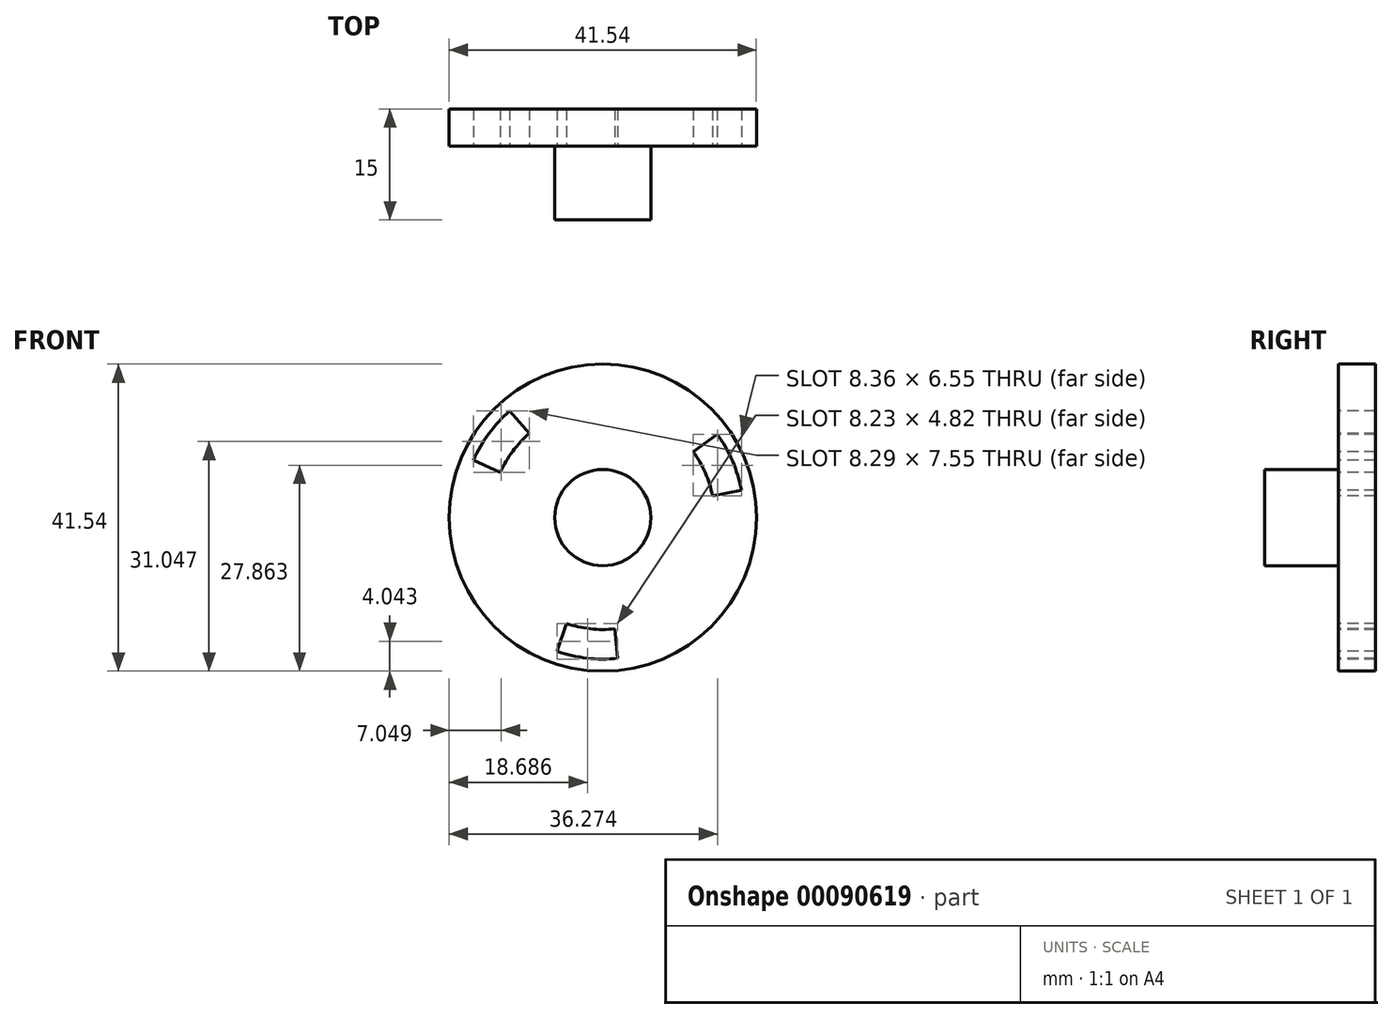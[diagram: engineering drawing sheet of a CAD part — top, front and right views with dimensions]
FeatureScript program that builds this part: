
annotation { "Feature Type Name" : "Feature", "Feature Type Description" : "" }
export const myFeature = defineFeature(function(context is Context, id is Id, definition is map)
    precondition{}
    {
        {
            var Q0;
            Q0=qCreatedBy(makeId("Front.planeOp"),FACE);
            var sketch = newSketch(context, id + "F0", { "sketchPlane" : qUnion([Q0])});
            skCircle(sketch, "E0", {"center": v(0, 0) * mm, "radius": 6.5 * mm});
            skSolve(sketch);
        }
        {
            var Q0;
            Q0 = qSketchRegion(id + "F0", true);
            extrude(context, id + "F1", {"entities" : qUnion([Q0]), "depth" : 10 * mm});
        }
        {
            var Q0;
            Q0=qCreatedBy(makeId("Front.planeOp"),FACE);
            var sketch = newSketch(context, id + "F2", { "sketchPlane" : qUnion([Q0])});
            skCircle(sketch, "E1", {"center": v(0, 0) * mm, "radius": 20.77 * mm});
            skSolve(sketch);
        }
        {
            var Q0;
            Q0=makeQuery(id+"F2.imprint","IMPRINT",FACE,{"disambiguationData":[TD([[makeQuery(id+"F2.imprint","IMPRINT",EDGE,{"derivedFrom":sQuery(id+"F2.wireOp",EDGE,"E1")}),1.0]])]});
            extrude(context, id + "F3", {"entities" : qUnion([Q0]), "operationType" : NewBodyOperationType.ADD, "oppositeDirection" : true, "depth" : 5 * mm});
        }
        {
            var Q0;
            Q0=makeQuery(id+"F3.opExtrude","CAP_FACE",FACE,{"disambiguationData":[OSD([sQuery(id+"F2.wireOp",EDGE,"E1")])],"isStart":true});
            var sketch = newSketch(context, id + "F4", { "sketchPlane" : qUnion([Q0])});
            skCircle(sketch, "E2", {"center": v(0, 0) * mm, "radius": 19.14 * mm});
            skCircle(sketch, "E3", {"center": v(0, 0) * mm, "radius": 15.14 * mm});
            skLineSegment(sketch, "E4", {"start": v(0, 0) * mm, "end": v(-13.66, 15.66) * mm});
            skLineSegment(sketch, "E5", {"start": v(0, 0) * mm, "end": v(-19, 8.42) * mm});
            skLineSegment(sketch, "E6", {"start": v(0, 0) * mm, "end": v(16.79, 12.24) * mm});
            skLineSegment(sketch, "E7", {"start": v(0, 0) * mm, "end": v(20.39, 4) * mm});
            skLineSegment(sketch, "E8", {"start": v(0, 0) * mm, "end": v(-6.73, -19.65) * mm});
            skLineSegment(sketch, "E9", {"start": v(0, 0) * mm, "end": v(2.2, -20.66) * mm});
            skSolve(sketch);
        }
        {
            var Q0;
            {var subQ0=sQuery(id+"F4.wireOp",EDGE,"E4");var subQ1=sQuery(id+"F4.wireOp",EDGE,"E2");var subQ2=makeQuery(id+"F4.imprint","INTERSECT",VERTEX,{"derivedFrom":[subQ1,subQ0]});Q0=makeQuery(id+"F4.imprint","IMPRINT",FACE,{"disambiguationData":[TD([[makeQuery(id+"F4.imprint","IMPRINT",EDGE,{"disambiguationData":[TD([[subQ2,-1.0]])],"derivedFrom":subQ1}),1.0]])]});}
            var Q1;
            {var subQ0=sQuery(id+"F4.wireOp",EDGE,"E6");var subQ1=sQuery(id+"F4.wireOp",EDGE,"E2");var subQ2=makeQuery(id+"F4.imprint","INTERSECT",VERTEX,{"derivedFrom":[subQ1,subQ0]});Q1=makeQuery(id+"F4.imprint","IMPRINT",FACE,{"disambiguationData":[TD([[makeQuery(id+"F4.imprint","IMPRINT",EDGE,{"disambiguationData":[TD([[subQ2,1.0]])],"derivedFrom":subQ1}),1.0]])]});}
            var Q2;
            {var subQ0=sQuery(id+"F4.wireOp",EDGE,"E8");var subQ1=sQuery(id+"F4.wireOp",EDGE,"E2");var subQ2=makeQuery(id+"F4.imprint","INTERSECT",VERTEX,{"derivedFrom":[subQ1,subQ0]});Q2=makeQuery(id+"F4.imprint","IMPRINT",FACE,{"disambiguationData":[TD([[makeQuery(id+"F4.imprint","IMPRINT",EDGE,{"disambiguationData":[TD([[subQ2,-1.0]])],"derivedFrom":subQ1}),1.0]])]});}
            extrude(context, id + "F5", {"entities" : qUnion([Q0, Q1, Q2]), "operationType" : NewBodyOperationType.REMOVE, "oppositeDirection" : true, "depth" : 25 * mm});
        }
    });
